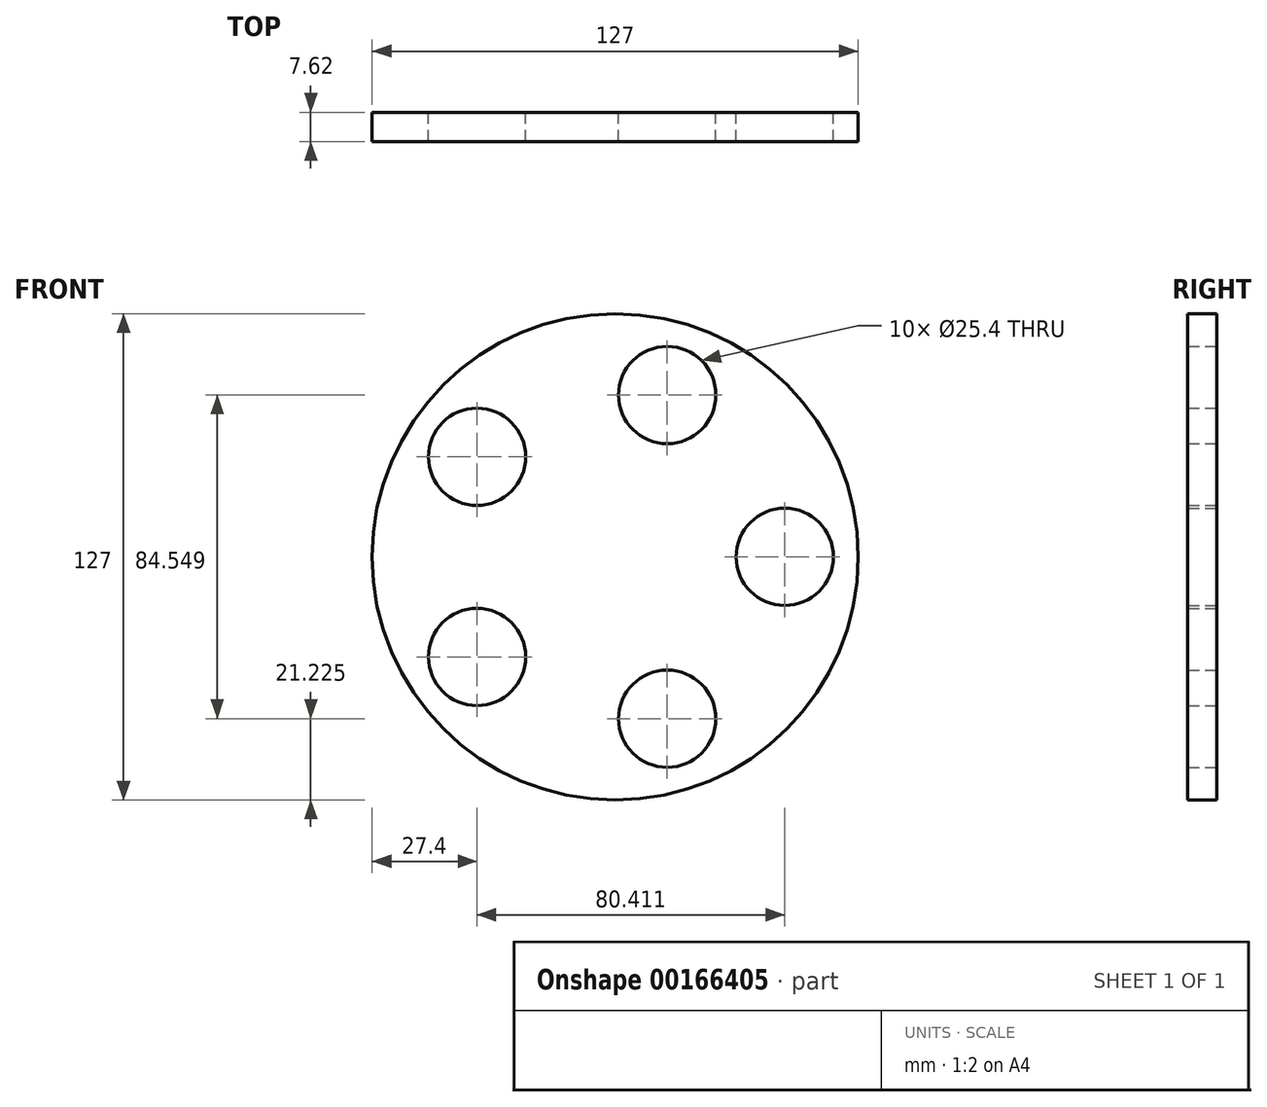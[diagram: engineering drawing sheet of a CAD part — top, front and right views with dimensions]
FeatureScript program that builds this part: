
annotation { "Feature Type Name" : "Feature", "Feature Type Description" : "" }
export const myFeature = defineFeature(function(context is Context, id is Id, definition is map)
    precondition{}
    {
        {
            var Q0;
            Q0=qCreatedBy(makeId("Front.planeOp"),FACE);
            var sketch = newSketch(context, id + "F0", { "sketchPlane" : qUnion([Q0])});
            skCircle(sketch, "E0", {"center": v(0, 0) * mm, "radius": 63.5 * mm});
            skCircle(sketch, "E1", {"center": v(44.31, 0) * mm, "radius": 12.7 * mm});
            skCircle(sketch, "E2.1.0", {"center": v(13.6, 42.27) * mm, "radius": 12.7 * mm});
            skCircle(sketch, "E2.2.0", {"center": v(-36.1, 26.13) * mm, "radius": 12.7 * mm});
            skCircle(sketch, "E2.3.0", {"center": v(-36.1, -26.13) * mm, "radius": 12.7 * mm});
            skCircle(sketch, "E2.4.0", {"center": v(13.6, -42.27) * mm, "radius": 12.7 * mm});
            skPoint(sketch, "E2.center", {"position": v(-0.14, 0) * mm});
            skSolve(sketch);
        }
        {
            var Q0;
            Q0=makeQuery(id+"F0.imprint","IMPRINT",FACE,{"disambiguationData":[TD([[makeQuery(id+"F0.imprint","IMPRINT",EDGE,{"derivedFrom":sQuery(id+"F0.wireOp",EDGE,"E0")}),1.0]])]});
            extrude(context, id + "F1", {"entities" : qUnion([Q0]), "depth" : 7.62 * mm});
        }
    });
